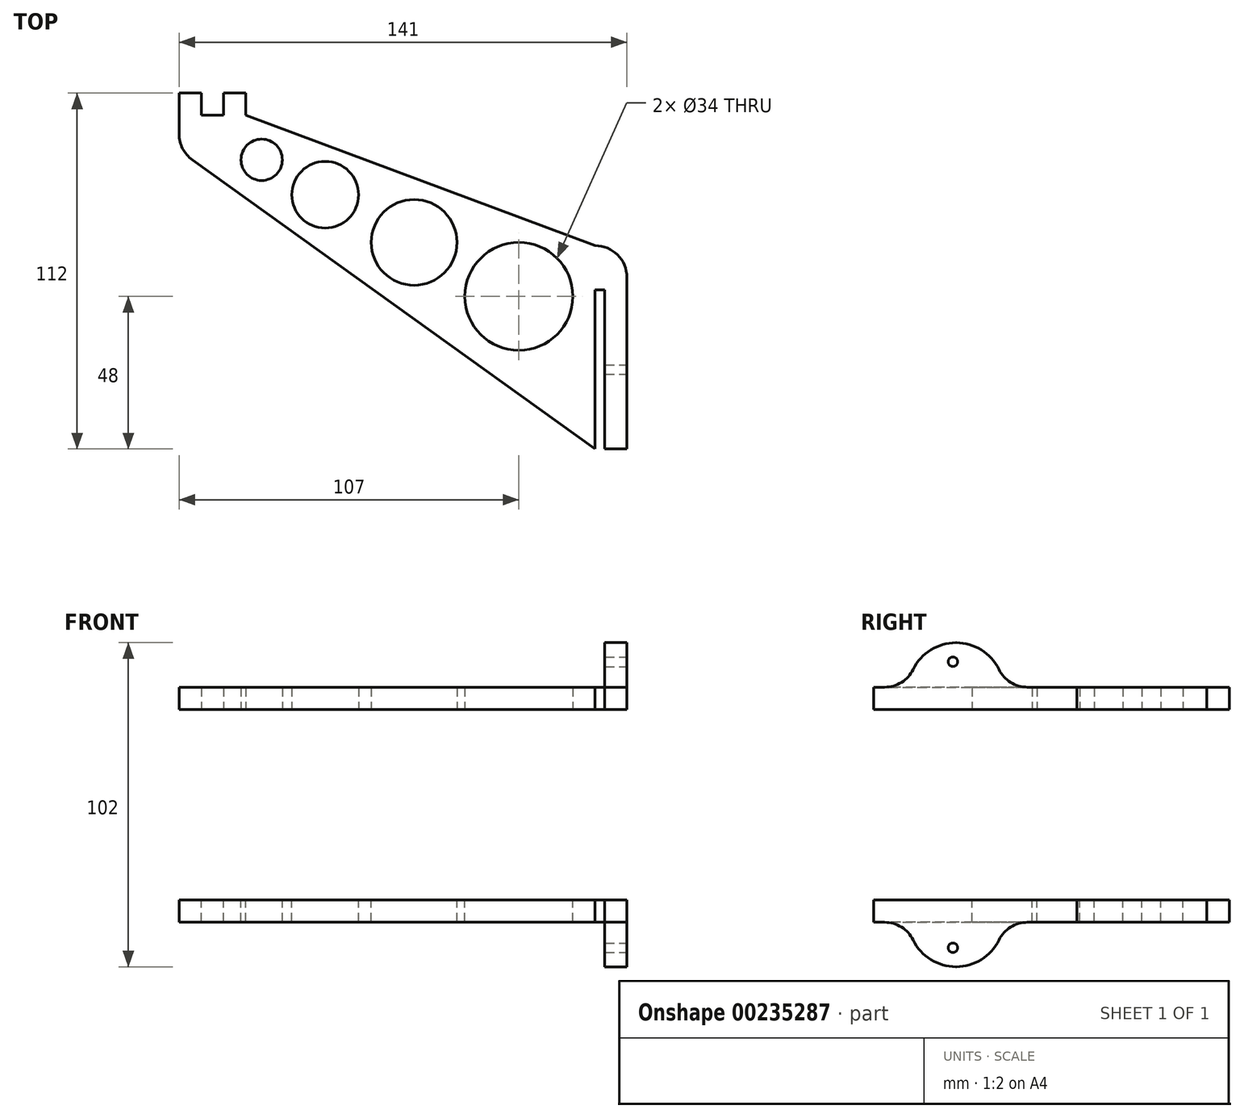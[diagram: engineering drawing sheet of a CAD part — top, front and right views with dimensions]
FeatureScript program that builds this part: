
annotation { "Feature Type Name" : "Feature", "Feature Type Description" : "" }
export const myFeature = defineFeature(function(context is Context, id is Id, definition is map)
    precondition{}
    {
        {
            var Q0;
            Q0=qCreatedBy(makeId("Top.planeOp"),FACE);
            var sketch = newSketch(context, id + "F0", { "sketchPlane" : qUnion([Q0])});
            skLineSegment(sketch, "E0", {"start": v(0, 0) * mm, "end": v(0, 64) * mm});
            skLineSegment(sketch, "E1", {"start": v(-120, 105) * mm, "end": v(-120, 112) * mm});
            skLineSegment(sketch, "E2", {"start": v(-120, 112) * mm, "end": v(-127, 112) * mm});
            skLineSegment(sketch, "E3", {"start": v(-127, 112) * mm, "end": v(-127, 105) * mm});
            skLineSegment(sketch, "E4", {"start": v(-127, 105) * mm, "end": v(-134, 105) * mm});
            skLineSegment(sketch, "E5", {"start": v(-134, 105) * mm, "end": v(-134, 112) * mm});
            skLineSegment(sketch, "E6", {"start": v(-134, 112) * mm, "end": v(-141, 112) * mm});
            skLineSegment(sketch, "E7", {"start": v(-141, 112) * mm, "end": v(-141, 94) * mm});
            skLineSegment(sketch, "E8", {"start": v(0, 0) * mm, "end": v(-7, 0) * mm});
            skLineSegment(sketch, "E9", {"start": v(-7, 0) * mm, "end": v(-7, 50) * mm});
            skLineSegment(sketch, "E10", {"start": v(-7, 50) * mm, "end": v(-10, 50) * mm});
            skLineSegment(sketch, "E11", {"start": v(-10, 50) * mm, "end": v(-10, 0) * mm});
            skLineSegment(sketch, "E12", {"start": v(-10, 0) * mm, "end": v(-141, 94) * mm});
            skLineSegment(sketch, "E13", {"start": v(0, 64) * mm, "end": v(-10, 64) * mm});
            skLineSegment(sketch, "E14", {"start": v(-10, 64) * mm, "end": v(-120, 105) * mm});
            skSolve(sketch);
        }
        {
            var Q0;
            Q0=qCreatedBy(makeId("Top.planeOp"),FACE);
            var sketch = newSketch(context, id + "F1", { "sketchPlane" : qUnion([Q0])});
            skCircle(sketch, "E15", {"center": v(-34, 48) * mm, "radius": 17 * mm});
            skCircle(sketch, "E16", {"center": v(-67, 65) * mm, "radius": 13.5 * mm});
            skCircle(sketch, "E17", {"center": v(-95, 80) * mm, "radius": 10.5 * mm});
            skCircle(sketch, "E18", {"center": v(-115, 91) * mm, "radius": 6.5 * mm});
            skSolve(sketch);
        }
        {
            var Q0;
            Q0 = qSketchRegion(id + "F0", true);
            extrude(context, id + "F2", {"entities" : qUnion([Q0]), "depth" : 7 * mm});
        }
        {
            var Q0;
            Q0 = qSketchRegion(id + "F1", true);
            extrude(context, id + "F3", {"entities" : qUnion([Q0]), "operationType" : NewBodyOperationType.REMOVE, "depth" : 25 * mm});
        }
        {
            var Q0;
            Q0=makeQuery(id+"F5miNz1vhawPfgH_1.boolean.opBoolean","MERGE",FACE,{"derivedFrom":[makeQuery(id+"F2.opExtrude","SWEPT_FACE",FACE,{"disambiguationData":[OSD([sQuery(id+"F0.wireOp",EDGE,"E0")])]}),makeQuery(id+"F5miNz1vhawPfgH_1.opExtrude","SWEPT_FACE",FACE,{"disambiguationData":[OSD([sQuery(id+"Fub9pXxP3nGjq5r_1.wireOp",EDGE,"dLX2nino-Qxha-NZRC-vta3-fouMhTpAGY63.right")])]})]});
            var sketch = newSketch(context, id + "F4", { "sketchPlane" : qUnion([Q0])});
            skLineSegment(sketch, "E19.bottom", {"start": v(41, 7) * mm, "end": v(11, 7) * mm});
            skLineSegment(sketch, "E19.top", {"start": v(41, 21) * mm, "end": v(11, 21) * mm});
            skLineSegment(sketch, "E19.left", {"start": v(41, 7) * mm, "end": v(41, 21) * mm});
            skLineSegment(sketch, "E19.right", {"start": v(11, 7) * mm, "end": v(11, 21) * mm});
            skSolve(sketch);
        }
        {
            var Q0;
            Q0 = qSketchRegion(id + "F4", true);
            extrude(context, id + "F5", {"entities" : qUnion([Q0]), "operationType" : NewBodyOperationType.ADD, "oppositeDirection" : true, "depth" : 7 * mm});
        }
        {
            var Q0;
            Q0=makeQuery(id+"F5.boolean.opBoolean","MERGE",FACE,{"derivedFrom":[makeQuery(id+"F2.opExtrude","SWEPT_FACE",FACE,{"disambiguationData":[OSD([sQuery(id+"F0.wireOp",EDGE,"E0")])]}),makeQuery(id+"F5.opExtrude","CAP_FACE",FACE,{"disambiguationData":[OSD([sQuery(id+"F4.wireOp",EDGE,"E19.bottom"),sQuery(id+"F4.wireOp",EDGE,"E19.top"),sQuery(id+"F4.wireOp",EDGE,"E19.left"),sQuery(id+"F4.wireOp",EDGE,"E19.right")])],"isStart":true})]});
            var sketch = newSketch(context, id + "F6", { "sketchPlane" : qUnion([Q0])});
            skCircle(sketch, "E20", {"center": v(25, 15) * mm, "radius": 1.5 * mm});
            skSolve(sketch);
        }
        {
            var Q0;
            Q0=makeQuery(id+"F5.opExtrude","SWEPT_EDGE",EDGE,{"disambiguationData":[OSD([sQuery(id+"F4.wireOp",EDGE,"E19.top"),sQuery(id+"F4.wireOp",EDGE,"E19.right")])]});
            var Q1;
            Q1=makeQuery(id+"F5.opExtrude","SWEPT_EDGE",EDGE,{"disambiguationData":[OSD([sQuery(id+"F4.wireOp",EDGE,"E19.top"),sQuery(id+"F4.wireOp",EDGE,"E19.left")])]});
            fillet(context, id + "F7", {"entities" : qUnion([Q0, Q1]), "radius" : 15 * mm, "tangentPropagation" : true, "allowEdgeOverflow" : false});
        }
        {
            var Q0;
            {var subQ0=sQuery(id+"F0.wireOp",EDGE,"E9");var subQ1=sQuery(id+"F0.wireOp",EDGE,"E8");var subQ2=sQuery(id+"F4.wireOp",EDGE,"E19.right");var subQ4=sQuery(id+"F4.wireOp",EDGE,"E19.top");var subQ6=sQuery(id+"F0.wireOp",EDGE,"E0");Q0=makeQuery(id+"F7.opFillet","BLEND_EDGE",EDGE,{"blendedFrom":[makeQuery(id+"F5.opExtrude","SWEPT_EDGE",EDGE,{"disambiguationData":[OSD([subQ4,subQ2])]}),makeQuery(id+"F5.boolean.opBoolean","SPLIT",FACE,{"disambiguationData":[TD([makeQuery(id+"F2.opExtrude","SWEPT_FACE",FACE,{"disambiguationData":[OSD([subQ1])]})])],"derivedFrom":makeQuery(id+"F2.opExtrude","CAP_FACE",FACE,{"disambiguationData":[OSD([subQ6,sQuery(id+"F0.wireOp",EDGE,"E1"),sQuery(id+"F0.wireOp",EDGE,"E2"),sQuery(id+"F0.wireOp",EDGE,"E3"),sQuery(id+"F0.wireOp",EDGE,"E4"),sQuery(id+"F0.wireOp",EDGE,"E5"),sQuery(id+"F0.wireOp",EDGE,"E6"),sQuery(id+"F0.wireOp",EDGE,"E7"),subQ1,subQ0,sQuery(id+"F0.wireOp",EDGE,"E10"),sQuery(id+"F0.wireOp",EDGE,"E11"),sQuery(id+"F0.wireOp",EDGE,"E12"),sQuery(id+"F0.wireOp",EDGE,"E13"),sQuery(id+"F0.wireOp",EDGE,"E14")])],"isStart":false})})],"blendedInto":[makeQuery(id+"F5.boolean.opBoolean","SPLIT",FACE,{"disambiguationData":[TD([makeQuery(id+"F2.opExtrude","SWEPT_FACE",FACE,{"disambiguationData":[OSD([subQ1])]})])],"derivedFrom":makeQuery(id+"F2.opExtrude","CAP_FACE",FACE,{"disambiguationData":[OSD([subQ6,sQuery(id+"F0.wireOp",EDGE,"E1"),sQuery(id+"F0.wireOp",EDGE,"E2"),sQuery(id+"F0.wireOp",EDGE,"E3"),sQuery(id+"F0.wireOp",EDGE,"E4"),sQuery(id+"F0.wireOp",EDGE,"E5"),sQuery(id+"F0.wireOp",EDGE,"E6"),sQuery(id+"F0.wireOp",EDGE,"E7"),subQ1,subQ0,sQuery(id+"F0.wireOp",EDGE,"E10"),sQuery(id+"F0.wireOp",EDGE,"E11"),sQuery(id+"F0.wireOp",EDGE,"E12"),sQuery(id+"F0.wireOp",EDGE,"E13"),sQuery(id+"F0.wireOp",EDGE,"E14")])],"isStart":false})})]});}
            var Q1;
            {var subQ0=sQuery(id+"F0.wireOp",EDGE,"E9");var subQ1=sQuery(id+"F0.wireOp",EDGE,"E4");var subQ2=sQuery(id+"F0.wireOp",EDGE,"E6");var subQ3=sQuery(id+"F0.wireOp",EDGE,"E5");var subQ4=sQuery(id+"F0.wireOp",EDGE,"E10");var subQ5=sQuery(id+"F0.wireOp",EDGE,"E0");var subQ6=sQuery(id+"F0.wireOp",EDGE,"E3");var subQ7=sQuery(id+"F0.wireOp",EDGE,"E12");var subQ9=sQuery(id+"F4.wireOp",EDGE,"E19.left");var subQ10=sQuery(id+"F4.wireOp",EDGE,"E19.top");var subQ12=sQuery(id+"F0.wireOp",EDGE,"E7");var subQ13=sQuery(id+"F0.wireOp",EDGE,"E2");var subQ14=sQuery(id+"F0.wireOp",EDGE,"E1");var subQ15=sQuery(id+"F0.wireOp",EDGE,"E11");var subQ16=sQuery(id+"F0.wireOp",EDGE,"E13");var subQ17=sQuery(id+"F0.wireOp",EDGE,"E14");Q1=makeQuery(id+"F7.opFillet","BLEND_EDGE",EDGE,{"blendedFrom":[makeQuery(id+"F5.opExtrude","SWEPT_EDGE",EDGE,{"disambiguationData":[OSD([subQ10,subQ9])]}),makeQuery(id+"F5.boolean.opBoolean","SPLIT",FACE,{"disambiguationData":[TD([makeQuery(id+"F2.opExtrude","SWEPT_FACE",FACE,{"disambiguationData":[OSD([subQ14])]})])],"derivedFrom":makeQuery(id+"F2.opExtrude","CAP_FACE",FACE,{"disambiguationData":[OSD([subQ5,subQ14,subQ13,subQ6,subQ1,subQ3,subQ2,subQ12,sQuery(id+"F0.wireOp",EDGE,"E8"),subQ0,subQ4,subQ15,subQ7,subQ16,subQ17])],"isStart":false})})],"blendedInto":[makeQuery(id+"F5.boolean.opBoolean","SPLIT",FACE,{"disambiguationData":[TD([makeQuery(id+"F2.opExtrude","SWEPT_FACE",FACE,{"disambiguationData":[OSD([subQ14])]})])],"derivedFrom":makeQuery(id+"F2.opExtrude","CAP_FACE",FACE,{"disambiguationData":[OSD([subQ5,subQ14,subQ13,subQ6,subQ1,subQ3,subQ2,subQ12,sQuery(id+"F0.wireOp",EDGE,"E8"),subQ0,subQ4,subQ15,subQ7,subQ16,subQ17])],"isStart":false})})]});}
            fillet(context, id + "F8", {"entities" : qUnion([Q0, Q1]), "radius" : 10 * mm, "tangentPropagation" : true, "allowEdgeOverflow" : false});
        }
        {
            var Q0;
            Q0 = qSketchRegion(id + "F6", true);
            extrude(context, id + "F9", {"entities" : qUnion([Q0]), "operationType" : NewBodyOperationType.REMOVE, "oppositeDirection" : true, "depth" : 25 * mm});
        }
        {
            var Q0;
            Q0=makeQuery(id+"F2.opExtrude","SWEPT_EDGE",EDGE,{"disambiguationData":[OSD([sQuery(id+"F0.wireOp",EDGE,"E0"),sQuery(id+"F0.wireOp",EDGE,"E13")])]});
            fillet(context, id + "F10", {"entities" : qUnion([Q0]), "radius" : 10 * mm, "tangentPropagation" : true, "allowEdgeOverflow" : false});
        }
        {
            var Q0;
            Q0=makeQuery(id+"F2.opExtrude","SWEPT_EDGE",EDGE,{"disambiguationData":[OSD([sQuery(id+"F0.wireOp",EDGE,"E7"),sQuery(id+"F0.wireOp",EDGE,"E12")])]});
            fillet(context, id + "F11", {"entities" : qUnion([Q0]), "radius" : 10 * mm, "tangentPropagation" : true, "allowEdgeOverflow" : false});
        }
        {
            var Q0;
            Q0=makeQuery(id+"F2.opExtrude","SWEPT_BODY",BODY,{"disambiguationData":[OSD([sQuery(id+"F0.wireOp",EDGE,"E0"),sQuery(id+"F0.wireOp",EDGE,"E1"),sQuery(id+"F0.wireOp",EDGE,"E2"),sQuery(id+"F0.wireOp",EDGE,"E3"),sQuery(id+"F0.wireOp",EDGE,"E4"),sQuery(id+"F0.wireOp",EDGE,"E5"),sQuery(id+"F0.wireOp",EDGE,"E6"),sQuery(id+"F0.wireOp",EDGE,"E7"),sQuery(id+"F0.wireOp",EDGE,"E8"),sQuery(id+"F0.wireOp",EDGE,"E9"),sQuery(id+"F0.wireOp",EDGE,"E10"),sQuery(id+"F0.wireOp",EDGE,"E11"),sQuery(id+"F0.wireOp",EDGE,"E12"),sQuery(id+"F0.wireOp",EDGE,"E13"),sQuery(id+"F0.wireOp",EDGE,"E14")])]});
            var Q1;
            Q1=qCreatedBy(makeId("Top.planeOp"),FACE);
            mirror(context, id + "F12", {"entities" : qUnion([Q0]), "mirrorPlane" : qUnion([Q1])});
        }
        {
            var Q0;
            Q0=makeQuery(id+"F12.opPattern","COPY",BODY,{"derivedFrom":makeQuery(id+"F2.opExtrude","SWEPT_BODY",BODY,{"disambiguationData":[OSD([sQuery(id+"F0.wireOp",EDGE,"E0"),sQuery(id+"F0.wireOp",EDGE,"E1"),sQuery(id+"F0.wireOp",EDGE,"E2"),sQuery(id+"F0.wireOp",EDGE,"E3"),sQuery(id+"F0.wireOp",EDGE,"E4"),sQuery(id+"F0.wireOp",EDGE,"E5"),sQuery(id+"F0.wireOp",EDGE,"E6"),sQuery(id+"F0.wireOp",EDGE,"E7"),sQuery(id+"F0.wireOp",EDGE,"E8"),sQuery(id+"F0.wireOp",EDGE,"E9"),sQuery(id+"F0.wireOp",EDGE,"E10"),sQuery(id+"F0.wireOp",EDGE,"E11"),sQuery(id+"F0.wireOp",EDGE,"E12"),sQuery(id+"F0.wireOp",EDGE,"E13"),sQuery(id+"F0.wireOp",EDGE,"E14")])]}),"instanceName":"1"});
            transform(context, id + "F13", {"entities" : qUnion([Q0]), "transformType" : TransformType.TRANSLATION_3D, "dx" : 0 * mm, "dy" : 0 * mm, "dz" : -60 * mm, "makeCopy" : false});
        }
    });
